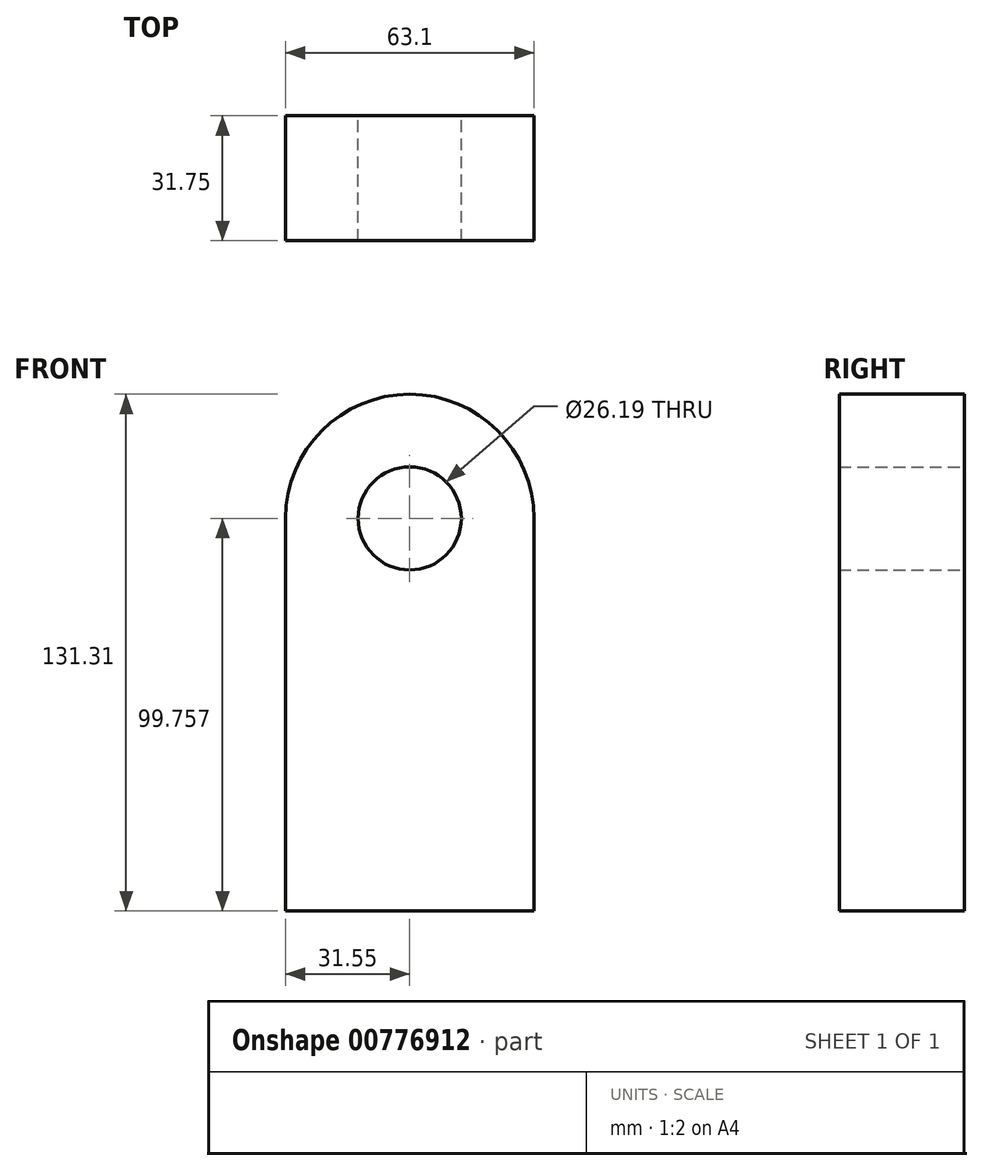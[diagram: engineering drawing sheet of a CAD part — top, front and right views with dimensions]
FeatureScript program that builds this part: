
annotation { "Feature Type Name" : "Feature", "Feature Type Description" : "" }
export const myFeature = defineFeature(function(context is Context, id is Id, definition is map)
    precondition{}
    {
        {
            var Q0;
            Q0=qCreatedBy(makeId("Front.planeOp"),FACE);
            var sketch = newSketch(context, id + "F0", { "sketchPlane" : qUnion([Q0])});
            skLineSegment(sketch, "E0.top", {"start": v(31.55, -49.88) * mm, "end": v(-31.55, -49.88) * mm});
            skLineSegment(sketch, "E0.left", {"start": v(31.55, 49.88) * mm, "end": v(31.55, -49.88) * mm});
            skLineSegment(sketch, "E0.right", {"start": v(-31.55, 49.88) * mm, "end": v(-31.55, -49.88) * mm});
            skPoint(sketch, "E0.middle", {"position": v(0, 0) * mm});
            skArc(sketch, "E1", {"start": v(31.55, 49.88) * mm, "mid": v(0, 81.43) * mm, "end": v(-31.55, 49.88) * mm});
            skCircle(sketch, "E2", {"center": v(0, 49.88) * mm, "radius": 13.1 * mm});
            skSolve(sketch);
        }
        {
            var Q0;
            Q0=makeQuery(id+"F0.imprint","IMPRINT",FACE,{"disambiguationData":[TD([[makeQuery(id+"F0.imprint","IMPRINT",EDGE,{"derivedFrom":sQuery(id+"F0.wireOp",EDGE,"E0.top")}),-1.0]])]});
            extrude(context, id + "F1", {"entities" : qUnion([Q0]), "depth" : 31.75 * mm, "offsetDistance" : 25.4 * mm});
        }
    });
